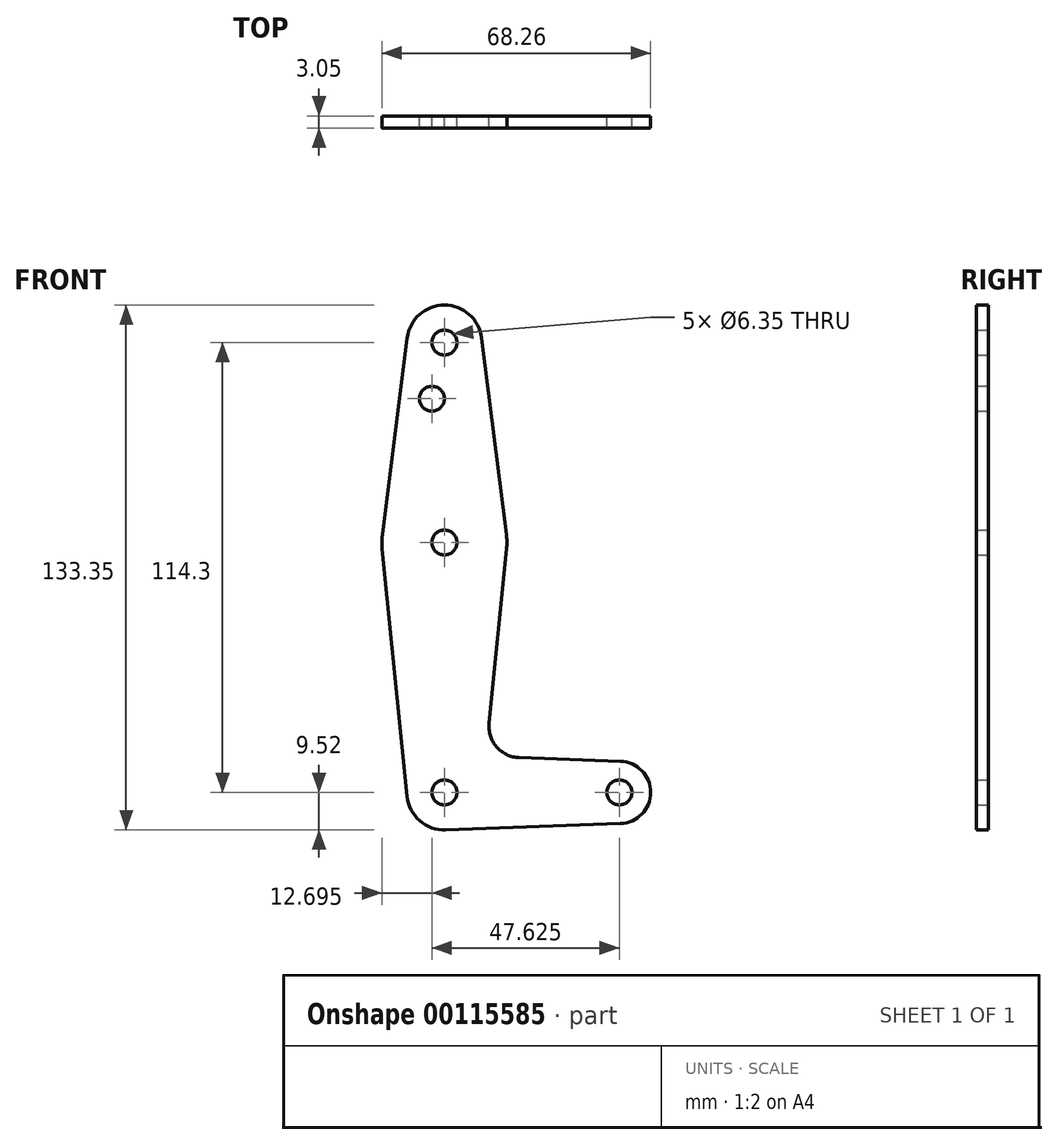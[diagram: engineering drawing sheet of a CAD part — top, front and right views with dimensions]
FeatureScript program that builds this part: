
annotation { "Feature Type Name" : "Feature", "Feature Type Description" : "" }
export const myFeature = defineFeature(function(context is Context, id is Id, definition is map)
    precondition{}
    {
        {
            var Q0;
            Q0=qCreatedBy(makeId("Front.planeOp"),FACE);
            var sketch = newSketch(context, id + "F0", { "sketchPlane" : qUnion([Q0])});
            skLineSegment(sketch, "E0", {"start": v(0, 0) * mm, "end": v(0, 114.3) * mm, "construction": true});
            skLineSegment(sketch, "E1", {"start": v(0, 0) * mm, "end": v(44.45, 0) * mm, "construction": true});
            skCircle(sketch, "E2", {"center": v(0, 0) * mm, "radius": 9.53 * mm});
            skCircle(sketch, "E3", {"center": v(0, 114.3) * mm, "radius": 9.53 * mm});
            skCircle(sketch, "E4", {"center": v(44.45, 0) * mm, "radius": 7.94 * mm});
            skCircle(sketch, "E5", {"center": v(0, 63.5) * mm, "radius": 15.88 * mm});
            skLineSegment(sketch, "E6", {"start": v(-9.45, 115.5) * mm, "end": v(-15.75, 65.48) * mm});
            skLineSegment(sketch, "E7", {"start": v(9.45, 115.5) * mm, "end": v(15.75, 65.48) * mm});
            skCircle(sketch, "E8", {"center": v(0, 114.3) * mm, "radius": 3.18 * mm});
            skCircle(sketch, "E9", {"center": v(0, 63.5) * mm, "radius": 3.18 * mm});
            skCircle(sketch, "E10", {"center": v(0, 0) * mm, "radius": 3.18 * mm});
            skCircle(sketch, "E11", {"center": v(44.45, 0) * mm, "radius": 3.18 * mm});
            skCircle(sketch, "E12", {"center": v(-3.18, 100.03) * mm, "radius": 3.18 * mm});
            skLineSegment(sketch, "E13", {"start": v(44.73, 7.93) * mm, "end": v(18.97, 8.85) * mm});
            skLineSegment(sketch, "E14", {"start": v(15.8, 61.91) * mm, "end": v(11.34, 17.6) * mm});
            skArc(sketch, "E15.filletArc", {"start": v(11.34, 17.6) * mm, "mid": v(13.26, 11.57) * mm, "end": v(18.97, 8.85) * mm});
            skLineSegment(sketch, "E16", {"start": v(-15.8, 61.91) * mm, "end": v(-9.48, -0.95) * mm});
            skLineSegment(sketch, "E17", {"start": v(0.34, -9.52) * mm, "end": v(44.73, -7.93) * mm});
            skSolve(sketch);
        }
        {
            var Q0;
            Q0 = qSketchRegion(id + "F0", true);
            extrude(context, id + "F1", {"entities" : qUnion([Q0]), "depth" : 3.05 * mm});
        }
    });
